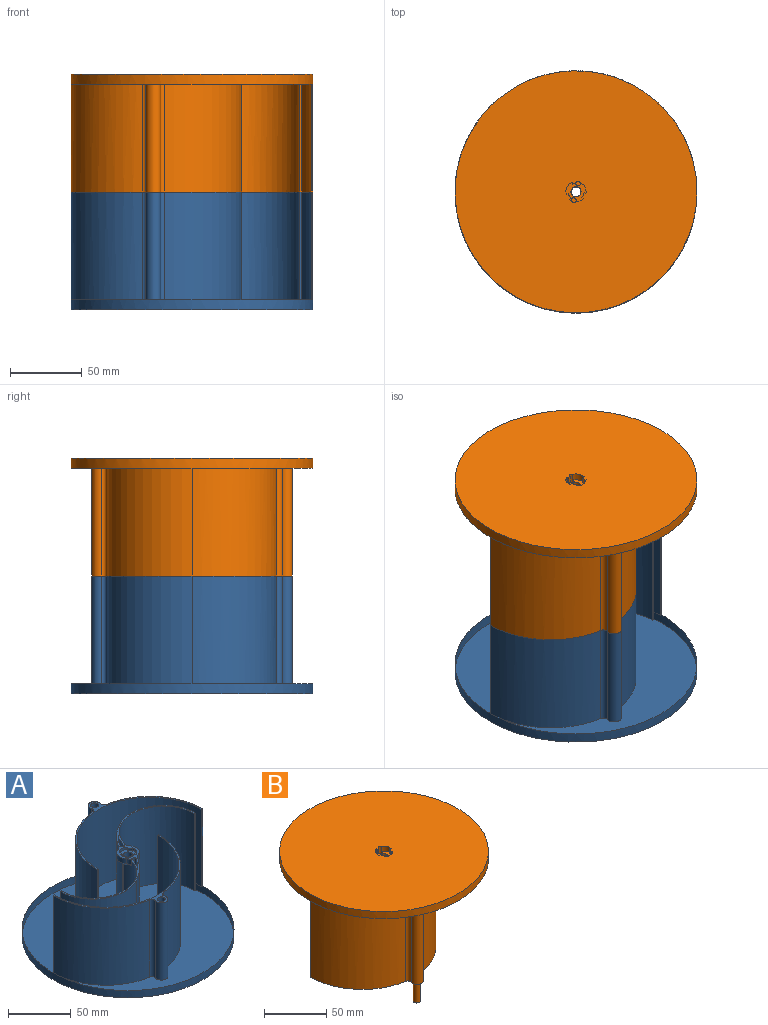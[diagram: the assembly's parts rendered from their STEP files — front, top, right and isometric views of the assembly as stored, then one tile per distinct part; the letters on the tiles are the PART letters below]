
ASSEMBLY  parts=2 mates=2
PART A: 93 faces, bbox 168.3x168.3x82 mm
  f0: cone r=10mm half-angle=45deg, axis (0,0,-1), area 6.3mm2, adj f2,f14,f84
  f1: cone r=10mm half-angle=45deg, axis (0,0,-1), area 3.2mm2, adj f3,f17,f85
  f2: cone r=4mm half-angle=45deg, axis (0,0,1), area 74.1mm2, adj f0,f4,f12,f13,f14,f69
  f3: cone r=4mm half-angle=45deg, axis (0,0,1), area 74.1mm2, adj f1,f5,f17,f18,f19,f68
  f4: cone r=10mm half-angle=45deg, axis (0,0,-1), area 3.2mm2, adj f2,f12,f83
  f5: cone r=10mm half-angle=45deg, axis (0,0,-1), area 6.3mm2, adj f3,f19,f86
  f6: plane 152.4x72.7mm, normal (0,0,1), area 427.1mm2, adj f11,f12,f14,f15,f16,f17,f19,f20
  f7: plane 168.33x168.33mm, normal (0,0,1), area 21120mm2, adj f8,f11,f12,f13,f14,f15,f16,f17
  f8: cylinder r=84.17mm len=168.33mm, axis (0,0,-1), area 3701.8mm2, adj f7,f63
  f9: cylinder r=3.5mm len=74.8mm, axis (0,0,-1), area 1644.9mm2, adj f10,f82
  f10: plane 14x13.74mm, normal (0,0,-1), area 99mm2, adj f9,f51,f52,f53,f54,f55,f56,f57
  f11: cylinder r=36.35mm len=75mm, axis (0,0,-1), area 5657.2mm2, adj f6,f7,f12,f24
  f12: cylinder r=60mm len=75mm, axis (0,0,-1), area 2999.6mm2, adj f2,f4,f6,f7,f11,f13,f83
  f13: cylinder r=4.7mm len=65.7mm, axis (0,0,-1), area 118.5mm2, adj f2,f7,f12,f14
  f14: cylinder r=35.15mm len=75mm, axis (0,0,-1), area 8209.7mm2, adj f0,f2,f6,f7,f13,f15,f84
  f15: plane 75x1.2mm, normal (0,1,0), area 90mm2, adj f6,f7,f14,f16
  f16: cylinder r=36.35mm len=75mm, axis (0,0,-1), area 5657.2mm2, adj f6,f7,f15,f17
  f17: cylinder r=60mm len=75mm, axis (0,0,-1), area 2999.6mm2, adj f1,f3,f6,f7,f16,f18,f85
  f18: cylinder r=4.7mm len=65.7mm, axis (0,0,-1), area 118.5mm2, adj f3,f7,f17,f19
  f19: cylinder r=35.15mm len=75mm, axis (0,0,-1), area 8209.7mm2, adj f3,f5,f6,f7,f18,f24,f86
  f20: cylinder r=1.76mm len=75mm, axis (0,0,-1), area 425.5mm2, adj f6,f21,f25,f27,f66,f67
  f21: cylinder r=58.8mm len=75mm, axis (0,0,-1), area 1130mm2, adj f6,f20,f25,f27
  f22: cylinder r=36.35mm len=75mm, axis (0,0,-1), area 1091.3mm2, adj f6,f23,f26,f28
  f23: cylinder r=1.76mm len=75mm, axis (0,0,-1), area 425.5mm2, adj f6,f22,f26,f28,f64,f65
  f24: plane 75x1.2mm, normal (0,-1,0), area 90mm2, adj f6,f7,f11,f19
  f25: cylinder r=36.35mm len=75mm, axis (0,0,-1), area 1091.3mm2, adj f6,f20,f21,f27
  f26: cylinder r=58.8mm len=75mm, axis (0,0,-1), area 1130mm2, adj f6,f22,f23,f28
  f27: plane 14.29x9.83mm, normal (0,0,1), area 28.7mm2, adj f20,f21,f25
  f28: plane 14.29x9.83mm, normal (0,0,1), area 28.7mm2, adj f22,f23,f26
  f29: plane 75x1.2mm, normal (0,-1,0), area 90mm2, adj f7,f30,f37,f38
  f30: cylinder r=59.31mm len=75mm, axis (0,0,-1), area 6288.9mm2, adj f7,f29,f31,f38
  f31: cylinder r=3mm len=75mm, axis (0,0,-1), area 399.4mm2, adj f7,f30,f32,f38
  f32: cylinder r=5.15mm len=75mm, axis (0,0,-1), area 1467.2mm2, adj f7,f31,f33,f38
  f33: cylinder r=3mm len=75mm, axis (0,0,-1), area 399.4mm2, adj f7,f32,f34,f38
  f34: cylinder r=59.31mm len=75mm, axis (0,0,-1), area 6582.6mm2, adj f7,f33,f35,f38
  f35: plane 75x1.2mm, normal (0,-1,0), area 90mm2, adj f7,f34,f37,f38
  f36: cylinder r=3.15mm len=75mm, axis (0,0,-1), area 1484.4mm2, adj f38,f39
  f37: cylinder r=58.12mm len=116.23mm, axis (0,0,-1), area 13693mm2, adj f7,f29,f35,f38
  f38: plane 118.63x69.58mm, normal (0,0,1), area 285.2mm2, adj f29,f30,f31,f32,f33,f34,f35,f36
  f39: plane 6.3x6.3mm, normal (0,0,1), area 31.2mm2, adj f36
  f40: plane 75x1.2mm, normal (0,1,0), area 90mm2, adj f7,f41,f48,f49
  f41: cylinder r=59.31mm len=75mm, axis (0,0,-1), area 6288.9mm2, adj f7,f40,f42,f49
  f42: cylinder r=3mm len=75mm, axis (0,0,-1), area 399.4mm2, adj f7,f41,f43,f49
  f43: cylinder r=5.15mm len=75mm, axis (0,0,-1), area 1467.2mm2, adj f7,f42,f44,f49
  f44: cylinder r=3mm len=75mm, axis (0,0,-1), area 399.4mm2, adj f7,f43,f45,f49
  f45: cylinder r=59.31mm len=75mm, axis (0,0,-1), area 6582.6mm2, adj f7,f44,f46,f49
  f46: plane 75x1.2mm, normal (0,1,0), area 90mm2, adj f7,f45,f48,f49
  f47: cylinder r=3.15mm len=75mm, axis (0,0,-1), area 1484.4mm2, adj f49,f50
  f48: cylinder r=58.12mm len=116.23mm, axis (0,0,-1), area 13693mm2, adj f7,f40,f46,f49
  f49: plane 118.63x69.58mm, normal (0,0,1), area 285.2mm2, adj f40,f41,f42,f43,f44,f45,f46,f47
  f50: plane 6.3x6.3mm, normal (0,0,1), area 31.2mm2, adj f47
  f51: cylinder r=5.65mm len=5mm, axis (0,0,1), area 20.4mm2, adj f10,f52,f62,f63
  f52: plane 5x1.42mm, normal (1,0.02,0), area 7.1mm2, adj f10,f51,f53,f63
  f53: cylinder r=7mm len=8.41mm, axis (0,0,1), area 53mm2, adj f10,f52,f54,f63
  f54: plane 5x1.22mm, normal (0.52,-0.86,0), area 7.1mm2, adj f10,f53,f55,f63
  f55: cylinder r=5.65mm len=5mm, axis (0,0,1), area 20.4mm2, adj f10,f54,f56,f63
  f56: plane 5x1.22mm, normal (-0.52,0.86,0), area 7.1mm2, adj f10,f55,f57,f63
  f57: cylinder r=7mm len=9.62mm, axis (0,0,1), area 53mm2, adj f10,f56,f58,f63
  f58: plane 5x1.25mm, normal (0.48,0.87,0), area 7.1mm2, adj f10,f57,f59,f63
  f59: cylinder r=5.65mm len=5mm, axis (0,0,1), area 20.4mm2, adj f10,f58,f60,f63
  f60: plane 5x1.25mm, normal (-0.48,-0.87,0), area 7.1mm2, adj f10,f59,f61,f63
  f61: cylinder r=7mm len=8.25mm, axis (0,0,1), area 53mm2, adj f10,f60,f62,f63
  f62: plane 5x1.42mm, normal (-1,-0.02,0), area 7.1mm2, adj f10,f51,f61,f63
  f63: plane 168.33x168.33mm, normal (0,0,-1), area 22116.8mm2, adj f8,f51,f52,f53,f54,f55,f56,f57
  f64: plane 2.46x0.99mm, normal (0,0,-1), area 1.2mm2, adj f23,f65
  f65: cylinder r=9mm len=10mm, axis (0,0,-1), area 25.8mm2, adj f6,f23,f64
  f66: plane 2.46x0.99mm, normal (0,0,-1), area 1.2mm2, adj f20,f67
  f67: cylinder r=9mm len=10mm, axis (0,0,-1), area 25.8mm2, adj f6,f20,f66
  f68: cylinder r=9mm len=14.2mm, axis (0,0,-1), area 87.6mm2, adj f3,f6,f85,f86
  f69: cylinder r=9mm len=14.2mm, axis (0,0,-1), area 87.6mm2, adj f2,f6,f83,f84
  f70: plane 2.2x1.42mm, normal (1,0.02,0), area 3.1mm2, adj f6,f71,f81,f82
  f71: cylinder r=5.65mm len=4mm, axis (0,0,-1), area 9mm2, adj f6,f70,f72,f82
  f72: plane 2.2x1.42mm, normal (-1,-0.02,0), area 3.1mm2, adj f6,f71,f73,f82
  f73: cylinder r=7mm len=8.25mm, axis (0,0,-1), area 23.3mm2, adj f6,f72,f74,f82
  f74: plane 2.2x1.25mm, normal (-0.48,-0.87,0), area 3.1mm2, adj f6,f73,f75,f82
  f75: cylinder r=5.65mm len=3.5mm, axis (0,0,-1), area 9mm2, adj f6,f74,f76,f82
  f76: plane 2.2x1.25mm, normal (0.48,0.87,0), area 3.1mm2, adj f6,f75,f77,f82
  f77: cylinder r=7mm len=9.62mm, axis (0,0,-1), area 23.3mm2, adj f6,f76,f78,f82
  f78: plane 2.2x1.22mm, normal (-0.52,0.86,0), area 3.1mm2, adj f6,f77,f79,f82
  f79: cylinder r=5.65mm len=3.43mm, axis (0,0,-1), area 9mm2, adj f6,f78,f80,f82
  f80: plane 2.2x1.22mm, normal (0.52,-0.86,0), area 3.1mm2, adj f6,f79,f81,f82
  f81: cylinder r=7mm len=8.41mm, axis (0,0,-1), area 23.3mm2, adj f6,f70,f80,f82
  f82: plane 14x13.74mm, normal (0,0,1), area 99mm2, adj f9,f70,f71,f72,f73,f74,f75,f76
  f83: cylinder r=5mm len=5mm, axis (0,0,-1), area 18.1mm2, adj f4,f6,f12,f69
  f84: cylinder r=5mm len=5mm, axis (0,0,1), area 24mm2, adj f0,f6,f14,f69
  f85: cylinder r=5mm len=5mm, axis (0,0,-1), area 18.1mm2, adj f1,f6,f17,f68
  f86: cylinder r=5mm len=5mm, axis (0,0,1), area 24mm2, adj f5,f6,f19,f68
  f87: plane 3.3x3.3mm, normal (0,0,-1), area 8.6mm2, adj f89
  f88: plane 3.3x3.3mm, normal (0,0,1), area 8.6mm2, adj f89
  f89: cylinder r=1.65mm len=65mm, axis (0,0,-1), area 673.9mm2, adj f87,f88
  f90: plane 3.3x3.3mm, normal (0,0,-1), area 8.6mm2, adj f92
  f91: plane 3.3x3.3mm, normal (0,0,1), area 8.6mm2, adj f92
  f92: cylinder r=1.65mm len=65mm, axis (0,0,-1), area 673.9mm2, adj f90,f91
PART B: 91 faces, bbox 168.3x168.3x102 mm
  f0: cone r=10mm half-angle=45deg, axis (0,0,1), area 3.2mm2, adj f2,f14,f87
  f1: cone r=10mm half-angle=45deg, axis (0,0,1), area 3.2mm2, adj f3,f19,f89
  f2: cone r=4mm half-angle=45deg, axis (0,0,-1), area 74.1mm2, adj f0,f4,f14,f15,f16,f73
  f3: cone r=4mm half-angle=45deg, axis (0,0,-1), area 74.1mm2, adj f1,f5,f19,f20,f21,f72
  f4: cone r=10mm half-angle=45deg, axis (0,0,1), area 6.3mm2, adj f2,f16,f88
  f5: cone r=10mm half-angle=45deg, axis (0,0,1), area 6.3mm2, adj f3,f21,f90
  f6: plane 152.4x72.7mm, normal (0,0,-1), area 427.1mm2, adj f13,f14,f16,f17,f18,f19,f21,f22
  f7: plane 14x13.67mm, normal (0,0,1), area 86.7mm2, adj f9,f10,f11,f55,f56,f57,f58,f59
  f8: plane 168.33x168.33mm, normal (0,0,-1), area 21120mm2, adj f12,f13,f14,f15,f16,f17,f18,f19
  f9: cylinder r=1.65mm len=62mm, axis (0,0,1), area 614.4mm2, adj f7,f53,f55,f66,f67
  f10: cylinder r=1.65mm len=62mm, axis (0,0,1), area 606.9mm2, adj f7,f54,f59,f60,f67
  f11: cylinder r=3.5mm len=74.8mm, axis (0,0,1), area 1644.9mm2, adj f7,f86
  f12: cylinder r=84.17mm len=168.33mm, axis (0,0,1), area 3701.8mm2, adj f8,f67
  f13: cylinder r=36.35mm len=75mm, axis (0,0,1), area 5657.2mm2, adj f6,f8,f14,f26
  f14: cylinder r=60mm len=75mm, axis (0,0,1), area 2999.6mm2, adj f0,f2,f6,f8,f13,f15,f87
  f15: cylinder r=4.7mm len=65.7mm, axis (0,0,1), area 118.5mm2, adj f2,f8,f14,f16
  f16: cylinder r=35.15mm len=75mm, axis (0,0,1), area 8209.7mm2, adj f2,f4,f6,f8,f15,f17,f88
  f17: plane 75x1.2mm, normal (0,1,0), area 90mm2, adj f6,f8,f16,f18
  f18: cylinder r=36.35mm len=75mm, axis (0,0,1), area 5657.2mm2, adj f6,f8,f17,f19
  f19: cylinder r=60mm len=75mm, axis (0,0,1), area 2999.6mm2, adj f1,f3,f6,f8,f18,f20,f89
  f20: cylinder r=4.7mm len=65.7mm, axis (0,0,1), area 118.5mm2, adj f3,f8,f19,f21
  f21: cylinder r=35.15mm len=75mm, axis (0,0,1), area 8209.7mm2, adj f3,f5,f6,f8,f20,f26,f90
  f22: cylinder r=1.76mm len=75mm, axis (0,0,1), area 425.5mm2, adj f6,f23,f27,f29,f70,f71
  f23: cylinder r=58.8mm len=75mm, axis (0,0,1), area 1130mm2, adj f6,f22,f27,f29
  f24: cylinder r=36.35mm len=75mm, axis (0,0,1), area 1091.3mm2, adj f6,f25,f28,f30
  f25: cylinder r=1.76mm len=75mm, axis (0,0,1), area 425.5mm2, adj f6,f24,f28,f30,f68,f69
  f26: plane 75x1.2mm, normal (0,-1,0), area 90mm2, adj f6,f8,f13,f21
  f27: cylinder r=36.35mm len=75mm, axis (0,0,1), area 1091.3mm2, adj f6,f22,f23,f29
  f28: cylinder r=58.8mm len=75mm, axis (0,0,1), area 1130mm2, adj f6,f24,f25,f30
  f29: plane 14.29x9.83mm, normal (0,0,-1), area 28.7mm2, adj f22,f23,f27
  f30: plane 14.29x9.83mm, normal (0,0,-1), area 28.7mm2, adj f24,f25,f28
  f31: plane 75x1.2mm, normal (0,-1,0), area 90mm2, adj f8,f32,f38,f39
  f32: cylinder r=59.31mm len=75mm, axis (0,0,1), area 6288.9mm2, adj f8,f31,f33,f39
  f33: cylinder r=3mm len=75mm, axis (0,0,1), area 399.4mm2, adj f8,f32,f34,f39
  f34: cylinder r=5.15mm len=75mm, axis (0,0,1), area 1467.2mm2, adj f8,f33,f35,f39
  f35: cylinder r=3mm len=75mm, axis (0,0,1), area 399.4mm2, adj f8,f34,f36,f39
  f36: cylinder r=59.31mm len=75mm, axis (0,0,1), area 6582.6mm2, adj f8,f35,f37,f39
  f37: plane 75x1.2mm, normal (0,-1,0), area 90mm2, adj f8,f36,f38,f39
  f38: cylinder r=58.12mm len=116.23mm, axis (0,0,1), area 13693mm2, adj f8,f31,f37,f39
  f39: plane 118.63x69.58mm, normal (0,0,-1), area 290.9mm2, adj f31,f32,f33,f34,f35,f36,f37,f38
  f40: plane 75x1.2mm, normal (0,1,0), area 90mm2, adj f8,f41,f47,f48
  f41: cylinder r=59.31mm len=75mm, axis (0,0,1), area 6288.9mm2, adj f8,f40,f42,f48
  f42: cylinder r=3mm len=75mm, axis (0,0,1), area 399.4mm2, adj f8,f41,f43,f48
  f43: cylinder r=5.15mm len=75mm, axis (0,0,1), area 1467.2mm2, adj f8,f42,f44,f48
  f44: cylinder r=3mm len=75mm, axis (0,0,1), area 399.4mm2, adj f8,f43,f45,f48
  f45: cylinder r=59.31mm len=75mm, axis (0,0,1), area 6582.6mm2, adj f8,f44,f46,f48
  f46: plane 75x1.2mm, normal (0,1,0), area 90mm2, adj f8,f45,f47,f48
  f47: cylinder r=58.12mm len=116.23mm, axis (0,0,1), area 13693mm2, adj f8,f40,f46,f48
  f48: plane 118.63x69.58mm, normal (0,0,-1), area 290.9mm2, adj f40,f41,f42,f43,f44,f45,f46,f47
  f49: cylinder r=2.85mm len=20mm, axis (0,0,1), area 358.1mm2, adj f48,f50
  f50: plane 5.7x5.7mm, normal (0,0,-1), area 25.5mm2, adj f49
  f51: cylinder r=2.85mm len=20mm, axis (0,0,1), area 358.1mm2, adj f39,f52
  f52: plane 5.7x5.7mm, normal (0,0,-1), area 25.5mm2, adj f51
  f53: plane 3.3x3.3mm, normal (0,0,1), area 8.6mm2, adj f9
  f54: plane 3.3x3.3mm, normal (0,0,1), area 8.6mm2, adj f10
  f55: cylinder r=7mm len=7.81mm, axis (0,0,-1), area 46.8mm2, adj f7,f9,f56,f67
  f56: plane 5x1.25mm, normal (0.48,0.87,0), area 7.1mm2, adj f7,f55,f57,f67
  f57: cylinder r=5.65mm len=5mm, axis (0,0,-1), area 20.4mm2, adj f7,f56,f58,f67
  f58: plane 5x1.25mm, normal (-0.48,-0.87,0), area 7.1mm2, adj f7,f57,f59,f67
  f59: cylinder r=7mm len=5.32mm, axis (0,0,-1), area 29.2mm2, adj f7,f10,f58,f67
  f60: cylinder r=7mm len=5mm, axis (0,0,-1), area 10.1mm2, adj f7,f10,f61,f67
  f61: plane 5x1.22mm, normal (0.52,-0.86,0), area 7.1mm2, adj f7,f60,f62,f67
  f62: cylinder r=5.65mm len=5mm, axis (0,0,-1), area 20.4mm2, adj f7,f61,f63,f67
  f63: plane 5x1.22mm, normal (-0.52,0.86,0), area 7.1mm2, adj f7,f62,f64,f67
  f64: cylinder r=7mm len=8.41mm, axis (0,0,-1), area 53mm2, adj f7,f63,f65,f67
  f65: plane 5x1.42mm, normal (-1,-0.02,0), area 7.1mm2, adj f7,f64,f66,f67
  f66: cylinder r=5.65mm len=5mm, axis (0,0,-1), area 10mm2, adj f7,f9,f65,f67
  f67: plane 168.33x168.33mm, normal (0,0,1), area 22112mm2, adj f9,f10,f12,f55,f56,f57,f58,f59
  f68: plane 2.46x0.99mm, normal (0,0,1), area 1.2mm2, adj f25,f69
  f69: cylinder r=9mm len=10mm, axis (0,0,1), area 25.8mm2, adj f6,f25,f68
  f70: plane 2.46x0.99mm, normal (0,0,1), area 1.2mm2, adj f22,f71
  f71: cylinder r=9mm len=10mm, axis (0,0,1), area 25.8mm2, adj f6,f22,f70
  f72: cylinder r=9mm len=14.2mm, axis (0,0,1), area 87.6mm2, adj f3,f6,f89,f90
  f73: cylinder r=9mm len=14.2mm, axis (0,0,1), area 87.6mm2, adj f2,f6,f87,f88
  f74: plane 2.2x1.25mm, normal (0.48,0.87,0), area 3.1mm2, adj f6,f75,f85,f86
  f75: cylinder r=7mm len=8.25mm, axis (0,0,1), area 23.3mm2, adj f6,f74,f76,f86
  f76: plane 2.2x1.42mm, normal (1,0.02,0), area 3.1mm2, adj f6,f75,f77,f86
  f77: cylinder r=5.65mm len=4mm, axis (0,0,1), area 9mm2, adj f6,f76,f78,f86
  f78: plane 2.2x1.42mm, normal (-1,-0.02,0), area 3.1mm2, adj f6,f77,f79,f86
  f79: cylinder r=7mm len=8.41mm, axis (0,0,1), area 23.3mm2, adj f6,f78,f80,f86
  f80: plane 2.2x1.22mm, normal (-0.52,0.86,0), area 3.1mm2, adj f6,f79,f81,f86
  f81: cylinder r=5.65mm len=3.43mm, axis (0,0,1), area 9mm2, adj f6,f80,f82,f86
  f82: plane 2.2x1.22mm, normal (0.52,-0.86,0), area 3.1mm2, adj f6,f81,f83,f86
  f83: cylinder r=7mm len=9.62mm, axis (0,0,1), area 23.3mm2, adj f6,f82,f84,f86
  f84: plane 2.2x1.25mm, normal (-0.48,-0.87,0), area 3.1mm2, adj f6,f83,f85,f86
  f85: cylinder r=5.65mm len=3.5mm, axis (0,0,1), area 9mm2, adj f6,f74,f84,f86
  f86: plane 14x13.74mm, normal (0,0,-1), area 99mm2, adj f11,f74,f75,f76,f77,f78,f79,f80
  f87: cylinder r=5mm len=5mm, axis (0,0,1), area 18.1mm2, adj f0,f6,f14,f73
  f88: cylinder r=5mm len=5mm, axis (0,0,-1), area 24mm2, adj f4,f6,f16,f73
  f89: cylinder r=5mm len=5mm, axis (0,0,1), area 18.1mm2, adj f1,f6,f19,f72
  f90: cylinder r=5mm len=5mm, axis (0,0,-1), area 24mm2, adj f5,f6,f21,f72
PLACE A at identity fixed
PLACE B t=(0,0,154)mm
MATE slider B.f34 <-> A.f32  axis (0,0,-1) through (26.98,64.43,77)mm
MATE slider B.f43 <-> A.f43  axis (0,0,-1) through (-26.98,-64.43,77)mm
